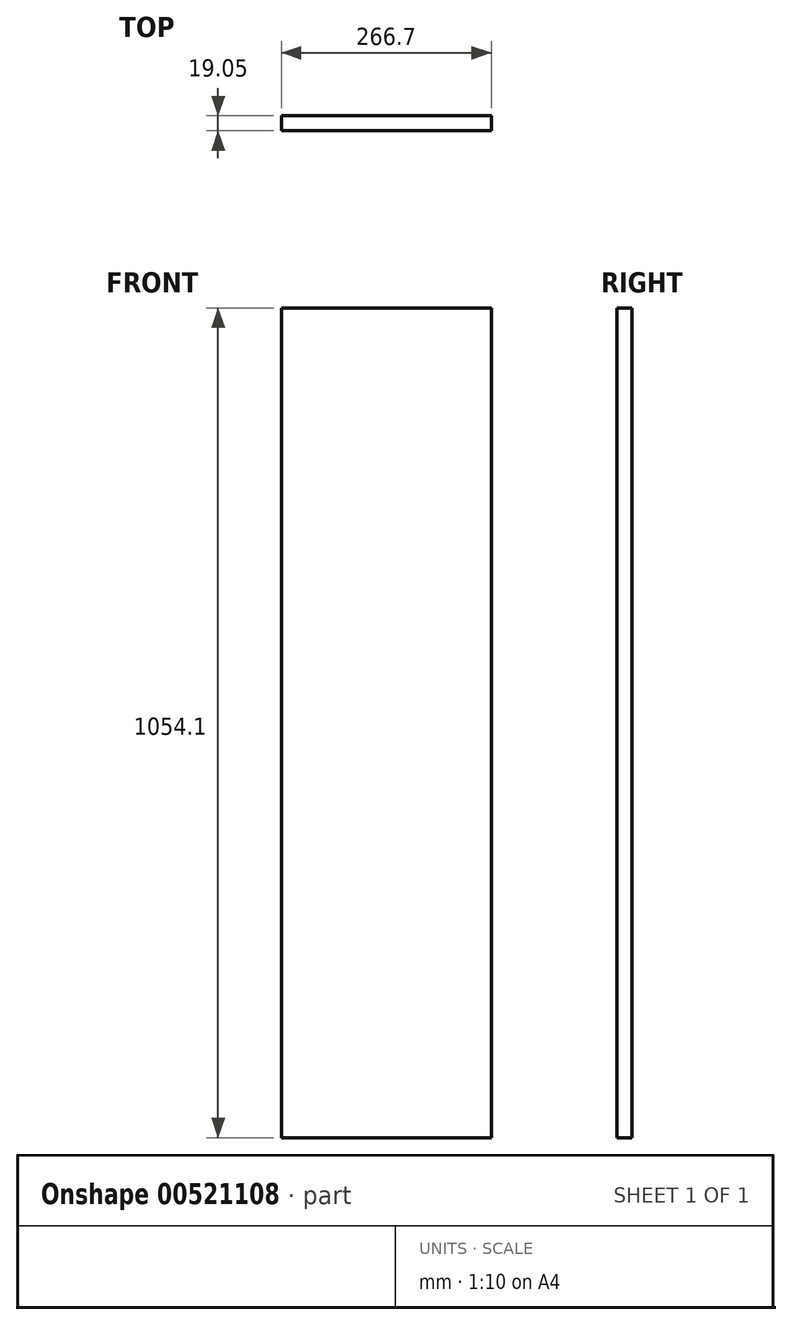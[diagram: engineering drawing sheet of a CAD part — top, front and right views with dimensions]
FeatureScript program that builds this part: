
annotation { "Feature Type Name" : "Feature", "Feature Type Description" : "" }
export const myFeature = defineFeature(function(context is Context, id is Id, definition is map)
    precondition{}
    {
        {
            var Q0;
            Q0=qCreatedBy(makeId("Front.planeOp"),FACE);
            var sketch = newSketch(context, id + "F0", { "sketchPlane" : qUnion([Q0])});
            skLineSegment(sketch, "E0.bottom", {"start": v(133.35, 527.05) * mm, "end": v(-133.35, 527.05) * mm});
            skLineSegment(sketch, "E0.top", {"start": v(133.35, -527.05) * mm, "end": v(-133.35, -527.05) * mm});
            skLineSegment(sketch, "E0.left", {"start": v(133.35, 527.05) * mm, "end": v(133.35, -527.05) * mm});
            skLineSegment(sketch, "E0.right", {"start": v(-133.35, 527.05) * mm, "end": v(-133.35, -527.05) * mm});
            skPoint(sketch, "E0.middle", {"position": v(0, 0) * mm});
            skSolve(sketch);
        }
        {
            var Q0;
            Q0=makeQuery(id+"F0.imprint","IMPRINT",FACE,{"disambiguationData":[TD([[makeQuery(id+"F0.imprint","IMPRINT",EDGE,{"derivedFrom":sQuery(id+"F0.wireOp",EDGE,"E0.bottom")}),1.0]])]});
            extrude(context, id + "F1", {"entities" : qUnion([Q0]), "depth" : 19.05 * mm, "offsetDistance" : 25.4 * mm});
        }
    });
